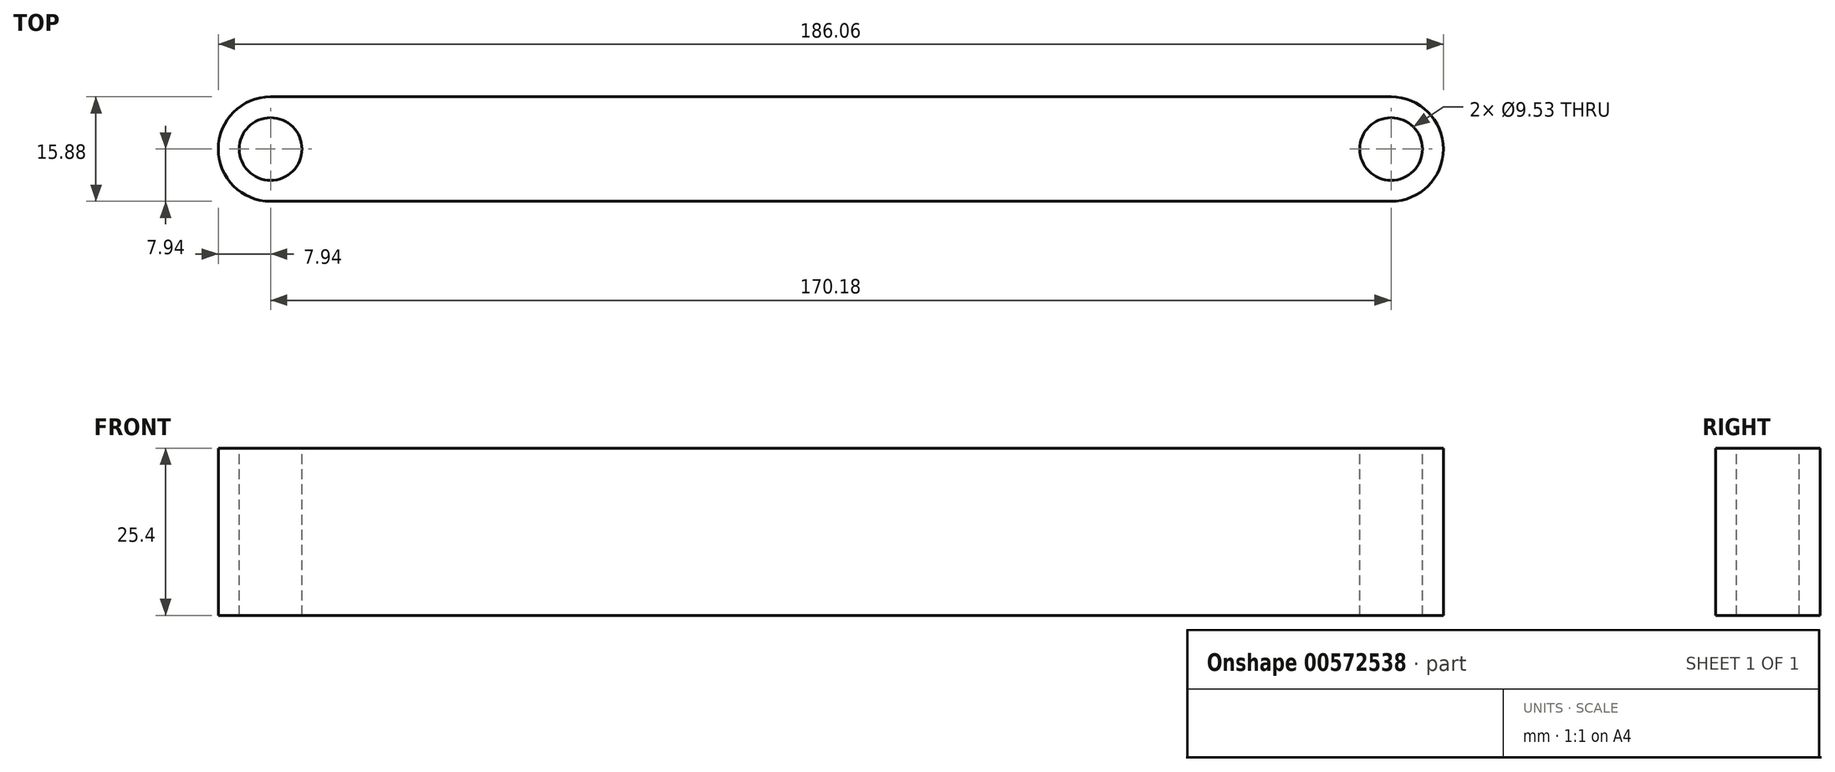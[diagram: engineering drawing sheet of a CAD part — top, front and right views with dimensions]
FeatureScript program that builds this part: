
annotation { "Feature Type Name" : "Feature", "Feature Type Description" : "" }
export const myFeature = defineFeature(function(context is Context, id is Id, definition is map)
    precondition{}
    {
        {
            var Q0;
            Q0=qCreatedBy(makeId("Top.planeOp"),FACE);
            var sketch = newSketch(context, id + "F0", { "sketchPlane" : qUnion([Q0])});
            skLineSegment(sketch, "E0.bottom", {"start": v(-93.03, 7.94) * mm, "end": v(93.03, 7.94) * mm});
            skLineSegment(sketch, "E0.top", {"start": v(-93.03, -7.94) * mm, "end": v(93.03, -7.94) * mm});
            skLineSegment(sketch, "E0.left", {"start": v(-93.03, 7.94) * mm, "end": v(-93.03, -7.94) * mm});
            skLineSegment(sketch, "E0.right", {"start": v(93.03, 7.94) * mm, "end": v(93.03, -7.94) * mm});
            skSolve(sketch);
        }
        {
            var Q0;
            Q0=makeQuery(id+"F0.imprint","IMPRINT",FACE,{"disambiguationData":[TD([[makeQuery(id+"F0.imprint","IMPRINT",EDGE,{"derivedFrom":sQuery(id+"F0.wireOp",EDGE,"E0.bottom")}),-1.0]])]});
            extrude(context, id + "F1", {"entities" : qUnion([Q0]), "depth" : 25.4 * mm, "offsetDistance" : 25.4 * mm});
        }
        {
            var Q0;
            Q0=makeQuery(id+"F1.opExtrude","SWEPT_EDGE",EDGE,{"disambiguationData":[OSD([sQuery(id+"F0.wireOp",EDGE,"E0.top"),sQuery(id+"F0.wireOp",EDGE,"E0.left")])]});
            var Q1;
            Q1=makeQuery(id+"F1.opExtrude","SWEPT_EDGE",EDGE,{"disambiguationData":[OSD([sQuery(id+"F0.wireOp",EDGE,"E0.bottom"),sQuery(id+"F0.wireOp",EDGE,"E0.left")])]});
            var Q2;
            Q2=makeQuery(id+"F1.opExtrude","SWEPT_EDGE",EDGE,{"disambiguationData":[OSD([sQuery(id+"F0.wireOp",EDGE,"E0.top"),sQuery(id+"F0.wireOp",EDGE,"E0.right")])]});
            var Q3;
            Q3=makeQuery(id+"F1.opExtrude","SWEPT_EDGE",EDGE,{"disambiguationData":[OSD([sQuery(id+"F0.wireOp",EDGE,"E0.bottom"),sQuery(id+"F0.wireOp",EDGE,"E0.right")])]});
            fillet(context, id + "F2", {"entities" : qUnion([Q0, Q1, Q2, Q3]), "radius" : 7.94 * mm, "tangentPropagation" : true, "allowEdgeOverflow" : false});
        }
        {
            var Q0;
            Q0=makeQuery(id+"F1.opExtrude","CAP_FACE",FACE,{"disambiguationData":[OSD([sQuery(id+"F0.wireOp",EDGE,"E0.bottom"),sQuery(id+"F0.wireOp",EDGE,"E0.top"),sQuery(id+"F0.wireOp",EDGE,"E0.left"),sQuery(id+"F0.wireOp",EDGE,"E0.right")])],"isStart":false});
            var sketch = newSketch(context, id + "F3", { "sketchPlane" : qUnion([Q0])});
            skPoint(sketch, "E1", {"position": v(85.1, 0) * mm});
            skPoint(sketch, "E2", {"position": v(-85.1, 0) * mm});
            skSolve(sketch);
        }
        {
            var Q0;
            Q0=sQuery(id+"F3.wireOp",VERTEX,"E2");
            var Q1;
            Q1=sQuery(id+"F3.wireOp",VERTEX,"E1");
            var Q2;
            Q2=makeQuery(id+"F1.opExtrude","SWEPT_BODY",BODY,{"disambiguationData":[OSD([sQuery(id+"F0.wireOp",EDGE,"E0.bottom"),sQuery(id+"F0.wireOp",EDGE,"E0.top"),sQuery(id+"F0.wireOp",EDGE,"E0.left"),sQuery(id+"F0.wireOp",EDGE,"E0.right")])]});
            hole(context, id + "F4", {"style" : HoleStyle.SIMPLE, "endStyle" : HoleEndStyle.THROUGH, "holeDiameter" : 9.52 * mm, "isTappedThrough" : true, "tappedDepth" : 12.7 * mm, "tapClearance" : 3, "locations" : qUnion([Q0, Q1]), "scope" : qUnion([Q2])});
        }
    });
